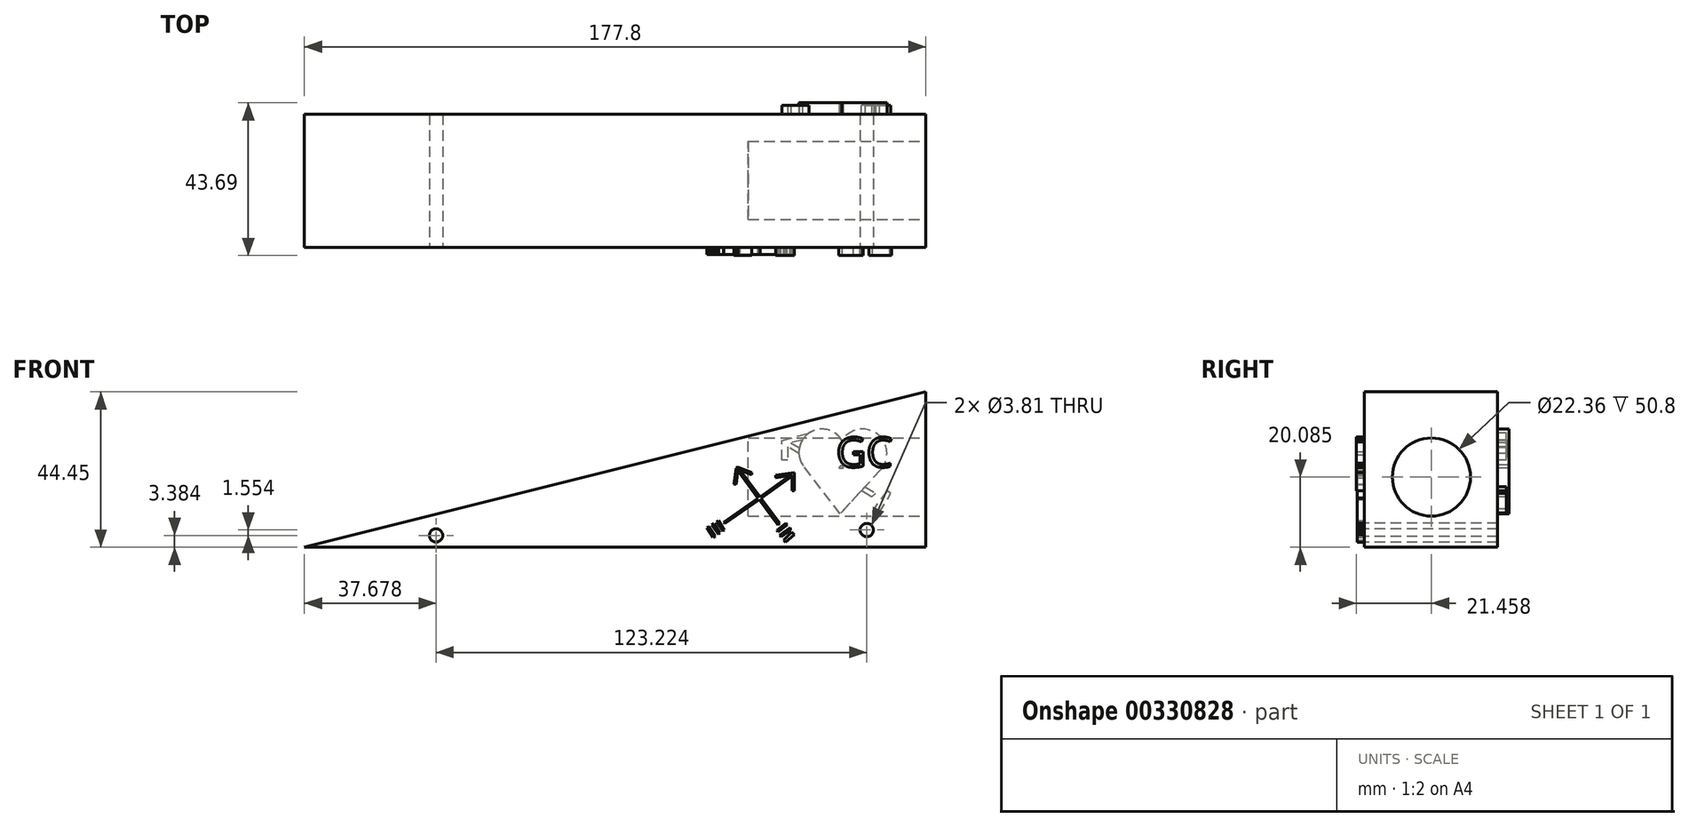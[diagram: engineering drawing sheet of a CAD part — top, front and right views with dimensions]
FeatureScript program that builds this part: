
annotation { "Feature Type Name" : "Feature", "Feature Type Description" : "" }
export const myFeature = defineFeature(function(context is Context, id is Id, definition is map)
    precondition{}
    {
        {
            var Q0;
            Q0=qCreatedBy(makeId("Front.planeOp"),FACE);
            var sketch = newSketch(context, id + "F0", { "sketchPlane" : qUnion([Q0])});
            skLineSegment(sketch, "E0", {"start": v(-93.31, 0) * mm, "end": v(84.49, 44.45) * mm});
            skLineSegment(sketch, "E1", {"start": v(84.49, 44.45) * mm, "end": v(84.49, 0) * mm});
            skLineSegment(sketch, "E2", {"start": v(84.49, 0) * mm, "end": v(-93.31, 0) * mm});
            skSolve(sketch);
        }
        {
            var Q0;
            Q0=makeQuery(id+"F0.imprint","IMPRINT",FACE,{"disambiguationData":[TD([[makeQuery(id+"F0.imprint","IMPRINT",EDGE,{"derivedFrom":sQuery(id+"F0.wireOp",EDGE,"E0")}),-1.0]])]});
            extrude(context, id + "F1", {"entities" : qUnion([Q0]), "depth" : 38.1 * mm});
        }
        {
            var Q0;
            Q0=makeQuery(id+"F1.opExtrude","CAP_FACE",FACE,{"disambiguationData":[OSD([sQuery(id+"F0.wireOp",EDGE,"E0"),sQuery(id+"F0.wireOp",EDGE,"E1"),sQuery(id+"F0.wireOp",EDGE,"E2")])],"isStart":false});
            var sketch = newSketch(context, id + "F2", { "sketchPlane" : qUnion([Q0])});
            skLineSegment(sketch, "E3", {"start": v(26.73, 7.15) * mm, "end": v(46.4, 21.01) * mm});
            skLineSegment(sketch, "E4", {"start": v(46.4, 21.01) * mm, "end": v(46.65, 20.66) * mm});
            skLineSegment(sketch, "E5", {"start": v(46.65, 20.66) * mm, "end": v(26.98, 6.8) * mm});
            skLineSegment(sketch, "E6", {"start": v(26.98, 6.8) * mm, "end": v(26.73, 7.15) * mm});
            skLineSegment(sketch, "E7", {"start": v(42.16, 6.38) * mm, "end": v(42.72, 6.84) * mm});
            skLineSegment(sketch, "E8", {"start": v(42.72, 6.84) * mm, "end": v(30.67, 22.98) * mm});
            skLineSegment(sketch, "E9", {"start": v(30.67, 22.98) * mm, "end": v(30.2, 22.63) * mm});
            skLineSegment(sketch, "E10", {"start": v(30.2, 22.63) * mm, "end": v(42.16, 6.38) * mm});
            skLineSegment(sketch, "E11", {"start": v(25.1, 7.61) * mm, "end": v(26.8, 4.85) * mm});
            skLineSegment(sketch, "E12", {"start": v(26.8, 4.85) * mm, "end": v(26.37, 4.59) * mm});
            skLineSegment(sketch, "E13", {"start": v(26.37, 4.59) * mm, "end": v(24.7, 7.29) * mm});
            skLineSegment(sketch, "E14", {"start": v(24.7, 7.29) * mm, "end": v(25.1, 7.61) * mm});
            skLineSegment(sketch, "E15", {"start": v(23.28, 6.4) * mm, "end": v(23.85, 6.76) * mm});
            skLineSegment(sketch, "E16", {"start": v(23.85, 6.76) * mm, "end": v(25.56, 4.08) * mm});
            skLineSegment(sketch, "E17", {"start": v(25.56, 4.08) * mm, "end": v(25.1, 3.78) * mm});
            skLineSegment(sketch, "E18", {"start": v(25.1, 3.78) * mm, "end": v(23.28, 6.4) * mm});
            skLineSegment(sketch, "E19", {"start": v(21.83, 5.58) * mm, "end": v(22.5, 5.9) * mm});
            skLineSegment(sketch, "E20", {"start": v(22.5, 5.9) * mm, "end": v(24.21, 3.18) * mm});
            skLineSegment(sketch, "E21", {"start": v(24.21, 3.18) * mm, "end": v(23.57, 2.78) * mm});
            skLineSegment(sketch, "E22", {"start": v(23.57, 2.78) * mm, "end": v(21.83, 5.58) * mm});
            skLineSegment(sketch, "E23", {"start": v(41.9, 4.85) * mm, "end": v(42.15, 4.37) * mm});
            skLineSegment(sketch, "E24", {"start": v(42.15, 4.37) * mm, "end": v(44.86, 6.4) * mm});
            skLineSegment(sketch, "E25", {"start": v(44.86, 6.4) * mm, "end": v(44.44, 6.95) * mm});
            skLineSegment(sketch, "E26", {"start": v(44.44, 6.95) * mm, "end": v(41.9, 4.85) * mm});
            skLineSegment(sketch, "E27", {"start": v(42.74, 3.45) * mm, "end": v(43.1, 2.95) * mm});
            skLineSegment(sketch, "E28", {"start": v(43.1, 2.95) * mm, "end": v(45.7, 4.85) * mm});
            skLineSegment(sketch, "E29", {"start": v(45.7, 4.85) * mm, "end": v(45.7, 5.58) * mm});
            skLineSegment(sketch, "E30", {"start": v(45.7, 5.58) * mm, "end": v(42.74, 3.45) * mm});
            skLineSegment(sketch, "E31", {"start": v(43.77, 2.1) * mm, "end": v(44.3, 1.45) * mm});
            skLineSegment(sketch, "E32", {"start": v(44.3, 1.45) * mm, "end": v(46.82, 3.55) * mm});
            skLineSegment(sketch, "E33", {"start": v(46.82, 3.55) * mm, "end": v(46.14, 4.37) * mm});
            skLineSegment(sketch, "E34", {"start": v(46.14, 4.37) * mm, "end": v(43.77, 2.1) * mm});
            skSolve(sketch);
        }
        {
            var Q0;
            {var subQ11=sQuery(id+"F2.wireOp",EDGE,"E4");Q0=makeQuery(id+"F2.imprint","IMPRINT",FACE,{"disambiguationData":[TD([[makeQuery(id+"F2.imprint","IMPRINT",EDGE,{"derivedFrom":subQ11}),1.0]])]});}
            var sketch = newSketch(context, id + "F3", { "sketchPlane" : qUnion([Q0])});
            skLineSegment(sketch, "E35", {"start": v(30.2, 22.68) * mm, "end": v(29.6, 18.05) * mm});
            skLineSegment(sketch, "E36", {"start": v(29.6, 18.05) * mm, "end": v(30.19, 17.97) * mm});
            skLineSegment(sketch, "E37", {"start": v(30.19, 17.97) * mm, "end": v(30.75, 22.26) * mm});
            skLineSegment(sketch, "E38", {"start": v(30.75, 22.26) * mm, "end": v(34.7, 20.71) * mm});
            skLineSegment(sketch, "E39", {"start": v(34.7, 20.71) * mm, "end": v(34.7, 21.44) * mm});
            skLineSegment(sketch, "E40", {"start": v(34.7, 21.44) * mm, "end": v(30.8, 22.95) * mm});
            skLineSegment(sketch, "E41", {"start": v(30.8, 22.95) * mm, "end": v(30.2, 22.68) * mm});
            skLineSegment(sketch, "E42", {"start": v(41.53, 20.58) * mm, "end": v(41.53, 19.84) * mm});
            skLineSegment(sketch, "E43", {"start": v(41.53, 19.84) * mm, "end": v(46.2, 20.57) * mm});
            skLineSegment(sketch, "E44", {"start": v(46.2, 20.57) * mm, "end": v(46.2, 16.2) * mm});
            skLineSegment(sketch, "E45", {"start": v(46.2, 16.2) * mm, "end": v(46.81, 16.2) * mm});
            skLineSegment(sketch, "E46", {"start": v(46.81, 16.2) * mm, "end": v(46.81, 21.33) * mm});
            skLineSegment(sketch, "E47", {"start": v(46.81, 21.33) * mm, "end": v(41.53, 20.58) * mm});
            skSolve(sketch);
        }
        {
            var Q0;
            Q0 = qSketchRegion(id + "F2", true);
            extrude(context, id + "F4", {"entities" : qUnion([Q0]), "operationType" : NewBodyOperationType.ADD, "depth" : 2.03 * mm});
        }
        {
            var Q0;
            Q0 = qSketchRegion(id + "F3", true);
            extrude(context, id + "F5", {"entities" : qUnion([Q0]), "operationType" : NewBodyOperationType.ADD, "depth" : 2.3 * mm});
        }
        {
            var Q0;
            Q0=makeQuery(id+"F1.opExtrude","SWEPT_FACE",FACE,{"disambiguationData":[OSD([sQuery(id+"F0.wireOp",EDGE,"E1")])]});
            var sketch = newSketch(context, id + "F6", { "sketchPlane" : qUnion([Q0])});
            skCircle(sketch, "E48", {"center": v(-18.93, 20.08) * mm, "radius": 11.18 * mm});
            skSolve(sketch);
        }
        {
            var Q0;
            Q0 = qSketchRegion(id + "F6", true);
            extrude(context, id + "F7", {"entities" : qUnion([Q0]), "operationType" : NewBodyOperationType.REMOVE, "oppositeDirection" : true, "depth" : 50.8 * mm});
        }
        {
            var Q0;
            Q0=makeQuery(id+"F1.opExtrude","CAP_FACE",FACE,{"disambiguationData":[OSD([sQuery(id+"F0.wireOp",EDGE,"E0"),sQuery(id+"F0.wireOp",EDGE,"E1"),sQuery(id+"F0.wireOp",EDGE,"E2")])],"isStart":false});
            var sketch = newSketch(context, id + "F8", { "sketchPlane" : qUnion([Q0])});
            skText(sketch, "E49", { "text": "GC", "fontName": "OpenSans-Regular.ttf"});
            const initialGuessF8  = {"E49": [0.05884, 0.02294, 1, 0, 0.00855]};
            skSetInitialGuess(sketch, initialGuessF8);
            skSolve(sketch);
        }
        {
            var Q0;
            Q0 = qSketchRegion(id + "F8", true);
            extrude(context, id + "F9", {"entities" : qUnion([Q0]), "operationType" : NewBodyOperationType.ADD, "depth" : 2.3 * mm});
        }
        {
            var Q0;
            Q0=makeQuery(id+"F1.opExtrude","CAP_FACE",FACE,{"disambiguationData":[OSD([sQuery(id+"F0.wireOp",EDGE,"E0"),sQuery(id+"F0.wireOp",EDGE,"E1"),sQuery(id+"F0.wireOp",EDGE,"E2")])],"isStart":true});
            var sketch = newSketch(context, id + "F10", { "sketchPlane" : qUnion([Q0])});
            skCircle(sketch, "E50", {"center": v(-66.4, 26.86) * mm, "radius": 6.95 * mm});
            skCircle(sketch, "E51", {"center": v(-54.8, 27.18) * mm, "radius": 6.62 * mm});
            skLineSegment(sketch, "E52", {"start": v(-71.53, 22.16) * mm, "end": v(-59.96, 9.55) * mm});
            skLineSegment(sketch, "E53", {"start": v(-59.96, 9.55) * mm, "end": v(-49.54, 23.16) * mm});
            skLineSegment(sketch, "E54", {"start": v(-49.54, 23.16) * mm, "end": v(-71.53, 22.16) * mm});
            skSolve(sketch);
        }
        {
            var Q0;
            Q0 = qSketchRegion(id + "F10", true);
            extrude(context, id + "F11", {"entities" : qUnion([Q0]), "operationType" : NewBodyOperationType.ADD, "depth" : 3.3 * mm});
        }
        {
            var Q0;
            {var subQ5=sQuery(id+"F0.wireOp",EDGE,"E2");var subQ7=sQuery(id+"F0.wireOp",EDGE,"E1");var subQ8=sQuery(id+"F0.wireOp",EDGE,"E0");Q0=makeQuery(id+"F11.boolean.opBoolean","SPLIT",FACE,{"disambiguationData":[TD([makeQuery(id+"F1.opExtrude","SWEPT_FACE",FACE,{"disambiguationData":[OSD([subQ8])]})])],"derivedFrom":makeQuery(id+"F1.opExtrude","CAP_FACE",FACE,{"disambiguationData":[OSD([subQ8,subQ7,subQ5])],"isStart":true})});}
            var sketch = newSketch(context, id + "F12", { "sketchPlane" : qUnion([Q0])});
            skLineSegment(sketch, "E55", {"start": v(-70.11, 15.46) * mm, "end": v(-68.9, 14.44) * mm});
            skLineSegment(sketch, "E56", {"start": v(-68.9, 14.44) * mm, "end": v(-44.11, 29.28) * mm});
            skLineSegment(sketch, "E57", {"start": v(-44.11, 29.28) * mm, "end": v(-44.86, 30.53) * mm});
            skLineSegment(sketch, "E58", {"start": v(-44.86, 30.53) * mm, "end": v(-70.11, 15.46) * mm});
            skLineSegment(sketch, "E59", {"start": v(-74.46, 15.46) * mm, "end": v(-73.43, 16.13) * mm});
            skLineSegment(sketch, "E60", {"start": v(-73.43, 16.13) * mm, "end": v(-69.58, 11.02) * mm});
            skLineSegment(sketch, "E61", {"start": v(-69.58, 11.02) * mm, "end": v(-71.18, 9.82) * mm});
            skLineSegment(sketch, "E62", {"start": v(-71.18, 9.82) * mm, "end": v(-74.46, 15.46) * mm});
            skLineSegment(sketch, "E63", {"start": v(-51.02, 31.13) * mm, "end": v(-45.9, 29.9) * mm});
            skLineSegment(sketch, "E64", {"start": v(-45.9, 29.9) * mm, "end": v(-45.02, 28.74) * mm});
            skLineSegment(sketch, "E65", {"start": v(-45.02, 28.74) * mm, "end": v(-45.02, 24.88) * mm});
            skLineSegment(sketch, "E66", {"start": v(-45.02, 24.88) * mm, "end": v(-43.38, 24.88) * mm});
            skLineSegment(sketch, "E67", {"start": v(-43.38, 24.88) * mm, "end": v(-43.38, 30.53) * mm});
            skLineSegment(sketch, "E68", {"start": v(-43.38, 30.53) * mm, "end": v(-51.1, 32.68) * mm});
            skLineSegment(sketch, "E69", {"start": v(-51.1, 32.68) * mm, "end": v(-51.02, 31.13) * mm});
            skSolve(sketch);
        }
        {
            var Q0;
            Q0 = qSketchRegion(id + "F12", true);
            extrude(context, id + "F13", {"entities" : qUnion([Q0]), "operationType" : NewBodyOperationType.ADD, "depth" : 2.54 * mm});
        }
        {
            var Q0;
            Q0=makeQuery(id+"F1.opExtrude","CAP_FACE",FACE,{"disambiguationData":[OSD([sQuery(id+"F0.wireOp",EDGE,"E0"),sQuery(id+"F0.wireOp",EDGE,"E1"),sQuery(id+"F0.wireOp",EDGE,"E2")])],"isStart":false});
            var sketch = newSketch(context, id + "F14", { "sketchPlane" : qUnion([Q0])});
            skCircle(sketch, "E70", {"center": v(-55.63, 3.38) * mm, "radius": 1.9 * mm});
            skSolve(sketch);
        }
        {
            var Q0;
            Q0=makeQuery(id+"F14.imprint","IMPRINT",FACE,{"disambiguationData":[TD([[makeQuery(id+"F14.imprint","IMPRINT",EDGE,{"derivedFrom":sQuery(id+"F14.wireOp",EDGE,"E70")}),-1.0]])]});
            var sketch = newSketch(context, id + "F15", { "sketchPlane" : qUnion([Q0])});
            skCircle(sketch, "E71", {"center": v(67.6, 4.94) * mm, "radius": 1.9 * mm});
            skSolve(sketch);
        }
        {
            var Q0;
            Q0=makeQuery(id+"F14.imprint","IMPRINT",FACE,{"disambiguationData":[TD([[makeQuery(id+"F14.imprint","IMPRINT",EDGE,{"derivedFrom":sQuery(id+"F14.wireOp",EDGE,"E70")}),1.0]])]});
            var Q1;
            Q1=makeQuery(id+"F15.imprint","IMPRINT",FACE,{"disambiguationData":[TD([[makeQuery(id+"F15.imprint","IMPRINT",EDGE,{"derivedFrom":sQuery(id+"F15.wireOp",EDGE,"E71")}),1.0]])]});
            var Q2;
            Q2=sQuery(id+"F15.wireOp",EDGE,"E71");
            var Q3;
            Q3=sQuery(id+"F14.wireOp",EDGE,"E70");
            extrude(context, id + "F16", {"entities" : qUnion([Q0, Q1]), "operationType" : NewBodyOperationType.REMOVE, "surfaceEntities" : qUnion([Q2, Q3]), "oppositeDirection" : true, "depth" : 58.17 * mm});
        }
    });
